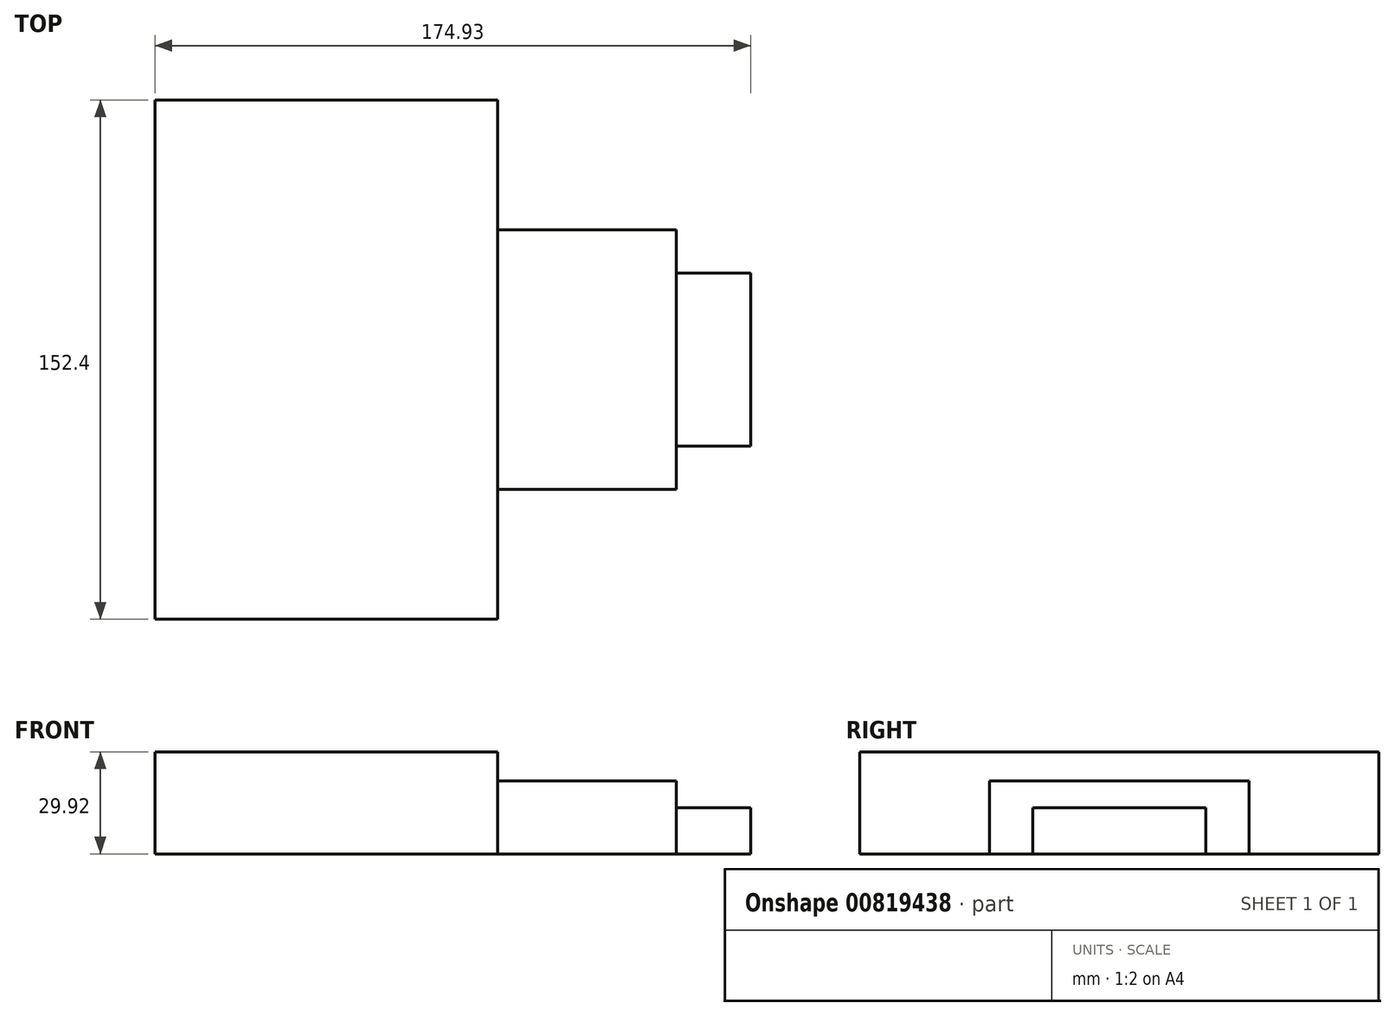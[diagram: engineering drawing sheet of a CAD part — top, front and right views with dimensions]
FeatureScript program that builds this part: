
annotation { "Feature Type Name" : "Feature", "Feature Type Description" : "" }
export const myFeature = defineFeature(function(context is Context, id is Id, definition is map)
    precondition{}
    {
        {
            var Q0;
            Q0=qCreatedBy(makeId("Top.planeOp"),FACE);
            var sketch = newSketch(context, id + "F0", { "sketchPlane" : qUnion([Q0])});
            skLineSegment(sketch, "E0.bottom", {"start": v(26.21, 38.1) * mm, "end": v(-26.21, 38.1) * mm});
            skLineSegment(sketch, "E0.top", {"start": v(26.21, -38.1) * mm, "end": v(-26.21, -38.1) * mm});
            skLineSegment(sketch, "E0.left", {"start": v(26.21, 38.1) * mm, "end": v(26.21, -38.1) * mm});
            skLineSegment(sketch, "E0.right", {"start": v(-26.21, 38.1) * mm, "end": v(-26.21, -38.1) * mm});
            skPoint(sketch, "E0.middle", {"position": v(0, 0) * mm});
            skLineSegment(sketch, "E1.bottom", {"start": v(-126.85, -76.2) * mm, "end": v(-26.21, -76.2) * mm});
            skLineSegment(sketch, "E1.top", {"start": v(-126.85, 76.2) * mm, "end": v(-26.21, 76.2) * mm});
            skLineSegment(sketch, "E1.left", {"start": v(-126.85, -76.2) * mm, "end": v(-126.85, 76.2) * mm});
            skLineSegment(sketch, "E1.right", {"start": v(-26.21, -76.2) * mm, "end": v(-26.21, 76.2) * mm});
            skLineSegment(sketch, "E2.bottom", {"start": v(26.21, -25.4) * mm, "end": v(48.08, -25.4) * mm});
            skLineSegment(sketch, "E2.top", {"start": v(26.21, 25.4) * mm, "end": v(48.08, 25.4) * mm});
            skLineSegment(sketch, "E2.left", {"start": v(26.21, -25.4) * mm, "end": v(26.21, 25.4) * mm});
            skLineSegment(sketch, "E2.right", {"start": v(48.08, -25.4) * mm, "end": v(48.08, 25.4) * mm});
            skSolve(sketch);
        }
        {
            var Q0;
            {var subQ2=sQuery(id+"F0.wireOp",EDGE,"E1.bottom");Q0=makeQuery(id+"F0.imprint","IMPRINT",FACE,{"disambiguationData":[TD([[makeQuery(id+"F0.imprint","IMPRINT",EDGE,{"derivedFrom":subQ2}),1.0]])]});}
            extrude(context, id + "F1", {"entities" : qUnion([Q0]), "depth" : 29.92 * mm, "offsetDistance" : 25.4 * mm});
        }
        {
            var Q0;
            {var subQ3=sQuery(id+"F0.wireOp",EDGE,"E0.bottom");Q0=makeQuery(id+"F0.imprint","IMPRINT",FACE,{"disambiguationData":[TD([[makeQuery(id+"F0.imprint","IMPRINT",EDGE,{"derivedFrom":subQ3}),1.0]])]});}
            extrude(context, id + "F2", {"entities" : qUnion([Q0]), "operationType" : NewBodyOperationType.ADD, "depth" : 21.36 * mm, "offsetDistance" : 25.4 * mm});
        }
        {
            var Q0;
            Q0=makeQuery(id+"F0.imprint","IMPRINT",FACE,{"disambiguationData":[TD([[makeQuery(id+"F0.imprint","IMPRINT",EDGE,{"derivedFrom":sQuery(id+"F0.wireOp",EDGE,"E2.bottom")}),1.0]])]});
            extrude(context, id + "F3", {"entities" : qUnion([Q0]), "operationType" : NewBodyOperationType.ADD, "depth" : 13.56 * mm, "offsetDistance" : 25.4 * mm});
        }
    });
